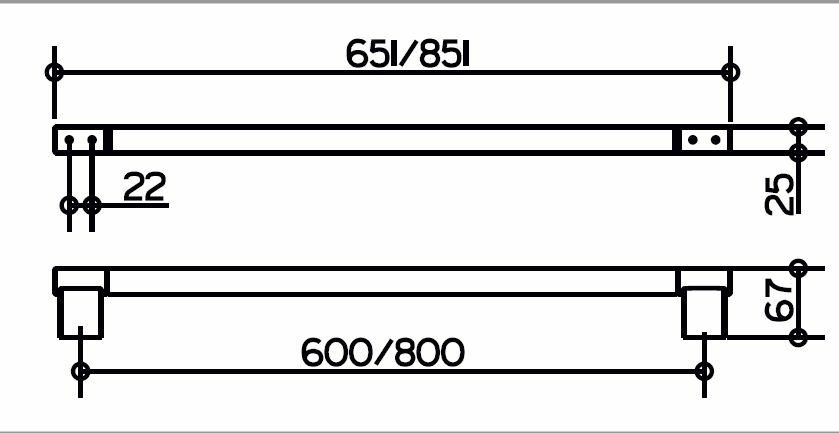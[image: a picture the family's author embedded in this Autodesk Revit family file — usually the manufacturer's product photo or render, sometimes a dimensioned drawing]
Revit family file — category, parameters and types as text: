
# Revit family: KEUCO_34914010611
name_source: partatom
category: Allgemeines Modell
revit_build: Autodesk Revit 2016 (Build: 20150220_1215(x64)
units: mm (PartAtom-declared; Revit-internal decimal feet)

## family parameters
Arbeitsebenenbasiert = Ja
Beim Laden mit Abzugskörper schneiden = Nein
Bemaßung runder Anschluss = Durchmesser verwenden
Gemeinsam genutzt = Nein
Immer vertikal = Nein
Kann Basisbauteil für Bewehrung sein = Nein
Raumberechnungspunkt = Nein
Teiletyp = Normal

## types (6) — shared parameters
Beschreibung = komplett mit Brauseschieber
Brausestange vor Montage frei positionierbar
Hersteller = KEUCO
Material Stange = 1222 mm  [stored 4.00919 ft]
Serie = Plan
URL = https://www.keuco.com
Verbindung = 40 mm  [stored 0.131234 ft]
Vorgabe-Ansicht = 1219 mm
zero-valued in all types: Gewicht

## per-type parameters (varying)
| type | Ausschreibungstext | Rail Length | Stange Material |
| 34914010611 | KEUCO PLAN CARE Duschhandlauf mit Brausestange 34914010611
hochglanzverchromter Duschhandlauf, T-Form
komplett mit Brauseschieber in ästhetischem,
funktionalem und ergonomischem Design,
die Brausestange ist vor der Montage frei positionierbar,
speziell für den Dusch- und Wannenbereich 
als Hilfe zum Festhalten und Abstützen,
bis 115 kg belastbar, antistatisch, leicht zu reinigen,
Außenmaße 682/1263 mm,
Achsmaß waagerecht 600 mm, senkrecht 1100 mm,
Rohrdurchmesser 33 mm, 4 Rosetten Durchmesser 82 mm,
Ausladung 90 mm, Wandabstand 57 mm,
Der Duschhandlauf wird verdeckt angebracht

Im Lieferumfang enthalten: 
4 x Befestigungs-Set 1 
Art.-Nr. 34990000100 (je 1 x pro Wandbefestigung) 

Der Handlauf ist Bauart geprüft

Der Griff ist kombinierbar mit dem Duschspritzschutz 34940 
und dem Klappsitz mit Rückenlehne 34981

Weitere Befestigungs-Sets
(je nach Ankergrund/Mauerwerk):
4 x Befestigungs-Set 4 (Art.-Nr. 34990000200) oder
4 x Befestigungs-Set 7 (Art.-Nr. 34993000200) | 680 mm  [stored 2.23097 ft] | Stahl, verchromt |
| 34914010911 | KEUCO PLAN CARE Duschhandlauf mit Brausestange 34914010911
hochglanzverchromter Duschhandlauf, T-Form,
komplett mit Brauseschieber in ästhetischem,
funktionalem und ergonomischem Design,
die Brausestange ist vor der Montage frei positionierbar,
speziell für den Dusch- und Wannenbereich 
als Hilfe zum Festhalten und Abstützen,
bis 115 kg belastbar, antistatisch, leicht zu reinigen,
Außenmaße 982/1263 mm,
Achsmaß waagerecht 900 mm, senkrecht 1100 mm,
Rohrdurchmesser 33 mm, 4 Rosetten Durchmesser 82 mm,
Ausladung 90 mm, Wandabstand 57 mm,
der Duschhandlauf wird verdeckt angebracht

Im Lieferumfang enthalten: 
4 x Befestigungs-Set 1 
Art.-Nr. 34990000100 (je 1 x pro Wandbefestigung) 

Der Handlauf ist Bauart geprüft

Der Griff ist kombinierbar mit dem Duschspritzschutz 34940 
und dem Klappsitz mit Rückenlehne 34981

Weitere Befestigungs-Sets
(je nach Ankergrund/Mauerwerk):
4 x Befestigungs-Set 4 (Art.-Nr. 34990000200) oder
4 x Befestigungs-Set 7 (Art.-Nr. 34993000200) | 980 mm  [stored 3.21522 ft] | Stahl, verchromt |
| 34914011111 | KEUCO PLAN CARE Duschhandlauf mit Brausestange 34914011111
hochglanzverchromter Duschhandlauf, T-Form,
komplett mit Brauseschieber in ästhetischem,
funktionalem und ergonomischem Design,
die Brausestange ist vor der Montage frei positionierbar,
speziell für den Dusch- und Wannenbereich 
als Hilfe zum Festhalten und Abstützen,
bis 115 kg belastbar, antistatisch, leicht zu reinigen,
Außenmaße 1182/1263 mm,
Achsmaß waagerecht 1100 mm, senkrecht 1100 mm,
Rohrdurchmesser 33 mm, 4 Rosetten Durchmesser 82 mm,
Ausladung 90 mm, Wandabstand 57 mm,
der Duschhandlauf wird verdeckt angebracht

Im Lieferumfang enthalten: 
4 x Befestigungs-Set 1 
Art.-Nr. 34990000100 (je 1 x pro Wandbefestigung) 

Der Handlauf ist Bauart geprüft

Der Griff ist kombinierbar mit dem Duschspritzschutz 34940 
und dem Klappsitz mit Rückenlehne 34981

Weitere Befestigungs-Sets
(je nach Ankergrund/Mauerwerk):
4 x Befestigungs-Set 4 (Art.-Nr. 34990000200) oder
4 x Befestigungs-Set 7 (Art.-Nr. 34993000200) | 1180 mm  [stored 3.87139 ft] | Stahl, verchromt |
| 34914170611 | KEUCO PLAN CARE Duschhandlauf mit Brausestange 34914170611
Duschhandlauf, T-Form,
Aluminium silber-eloxiert (E6 EV1)/verchromt,
komplett mit Brauseschieber in ästhetischem,
funktionalem und ergonomischem Design,
die Brausestange ist vor der Montage frei positionierbar,
speziell für den Dusch- und Wannenbereich 
als Hilfe zum Festhalten und Abstützen,
bis 115 kg belastbar, antistatisch, leicht zu reinigen,
Außenmaße 682/1263 mm,
Achsmaß waagerecht 600 mm, senkrecht 1100 mm,
Rohrdurchmesser 33 mm, 4 Rosetten Durchmesser 82 mm,
Ausladung 90 mm, Wandabstand 57 mm,
der Duschhandlauf wird verdeckt angebracht

Im Lieferumfang enthalten: 
4 x Befestigungs-Set 1 
Art.-Nr. 34990000100 (je 1 x pro Wandbefestigung) 

Der Handlauf ist Bauart geprüft

Der Griff ist kombinierbar mit dem Duschspritzschutz 34940 
und dem Klappsitz mit Rückenlehne 34981

Weitere Befestigungs-Sets
(je nach Ankergrund/Mauerwerk):
4 x Befestigungs-Set 4 (Art.-Nr. 34990000200) oder
4 x Befestigungs-Set 7 (Art.-Nr. 34993000200) | 680 mm  [stored 2.23097 ft] | Stahl, verchromt |
| 34914170911 | KEUCO PLAN CARE Duschhandlauf mit Brausestange 34914170911
Duschhandlauf, T-Form,
Aluminium silber-eloxiert (E6 EV1)/verchromt,
komplett mit Brauseschieber in ästhetischem,
funktionalem und ergonomischem Design,
die Brausestange ist vor der Montage frei positionierbar,
speziell für den Dusch- und Wannenbereich 
als Hilfe zum Festhalten und Abstützen,
bis 115 kg belastbar, antistatisch, leicht zu reinigen,
Außenmaße 982/1263 mm,
Achsmaß waagerecht 900 mm, senkrecht 1100 mm,
Rohrdurchmesser 33 mm, 4 Rosetten Durchmesser 82 mm,
Ausladung 90 mm, Wandabstand 57 mm,
der Duschhandlauf wird verdeckt angebracht

Im Lieferumfang enthalten: 
4 x Befestigungs-Set 1 
Art.-Nr. 34990000100 (je 1 x pro Wandbefestigung) 

Der Handlauf ist Bauart geprüft

Der Griff ist kombinierbar mit dem Duschspritzschutz 34940 
und dem Klappsitz mit Rückenlehne 34981

Weitere Befestigungs-Sets
(je nach Ankergrund/Mauerwerk):
4 x Befestigungs-Set 4 (Art.-Nr. 34990000200) oder
4 x Befestigungs-Set 7 (Art.-Nr. 34993000200) | 980 mm  [stored 3.21522 ft] | Aluminium 1100-H18 |
| 34914171111 | KEUCO PLAN CARE Duschhandlauf mit Brausestange 34914171111
Duschhandlauf, T-Form,
Aluminium silber-eloxiert (E6 EV1)/verchromt,
komplett mit Brauseschieber in ästhetischem,
funktionalem und ergonomischem Design,
die Brausestange ist vor der Montage frei positionierbar,
speziell für den Dusch- und Wannenbereich 
als Hilfe zum Festhalten und Abstützen,
bis 115 kg belastbar, antistatisch, leicht zu reinigen,
Außenmaße 1182/1263 mm,
Achsmaß waagerecht 1100 mm, senkrecht 1100 mm,
Rohrdurchmesser 33 mm, 4 Rosetten Durchmesser 82 mm,
Ausladung 90 mm, Wandabstand 57 mm,
der Duschhandlauf wird verdeckt angebracht

Im Lieferumfang enthalten: 
4 x Befestigungs-Set 1 
Art.-Nr. 34990000100 (je 1 x pro Wandbefestigung) 

Der Handlauf ist Bauart geprüft

Der Griff ist kombinierbar mit dem Duschspritzschutz 34940 
und dem Klappsitz mit Rückenlehne 34981

Weitere Befestigungs-Sets
(je nach Ankergrund/Mauerwerk):
4 x Befestigungs-Set 4 (Art.-Nr. 34990000200) oder
4 x Befestigungs-Set 7 (Art.-Nr. 34993000200) | 1180 mm  [stored 3.87139 ft] | Aluminium 1100-H18 |

note: column(s) folded — value = type name in every type: Artikelnummer

note: [stored X ft] marks values corroborated as IEEE doubles in the binary element streams (Revit-internal decimal feet)

## geometry (parser evidence)
native form markers: Sweep x3
no freeform markers — native parametric forms only
